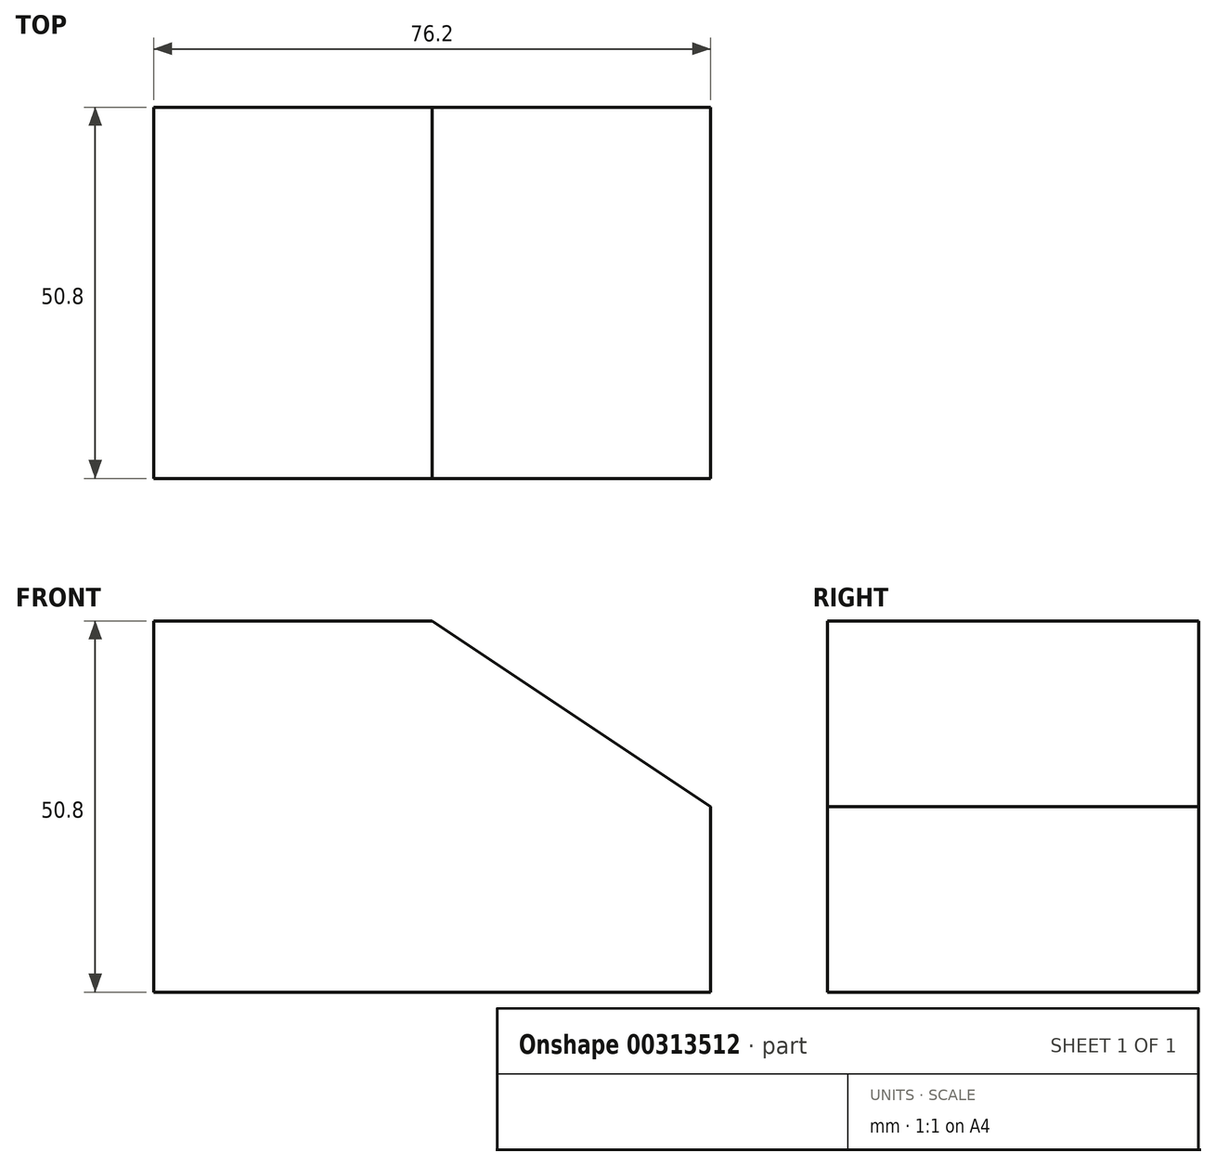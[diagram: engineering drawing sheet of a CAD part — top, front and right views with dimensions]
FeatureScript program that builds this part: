
annotation { "Feature Type Name" : "Feature", "Feature Type Description" : "" }
export const myFeature = defineFeature(function(context is Context, id is Id, definition is map)
    precondition{}
    {
        {
            var Q0;
            Q0=qCreatedBy(makeId("Front.planeOp"),FACE);
            var sketch = newSketch(context, id + "F0", { "sketchPlane" : qUnion([Q0])});
            skLineSegment(sketch, "E0", {"start": v(-38.1, -45.19) * mm, "end": v(38.1, -45.19) * mm});
            skLineSegment(sketch, "E1", {"start": v(38.1, -45.19) * mm, "end": v(38.1, -19.79) * mm});
            skLineSegment(sketch, "E2", {"start": v(-38.1, -45.19) * mm, "end": v(-38.1, 5.61) * mm});
            skLineSegment(sketch, "E3", {"start": v(-38.1, 5.61) * mm, "end": v(0, 5.61) * mm});
            skLineSegment(sketch, "E4", {"start": v(0, 5.61) * mm, "end": v(38.1, -19.79) * mm});
            skSolve(sketch);
        }
        {
            var Q0;
            Q0=makeQuery(id+"F0.imprint","IMPRINT",FACE,{"disambiguationData":[TD([[makeQuery(id+"F0.imprint","IMPRINT",EDGE,{"derivedFrom":sQuery(id+"F0.wireOp",EDGE,"E0")}),1.0]])]});
            extrude(context, id + "F1", {"entities" : qUnion([Q0]), "depth" : 50.8 * mm});
        }
    });
